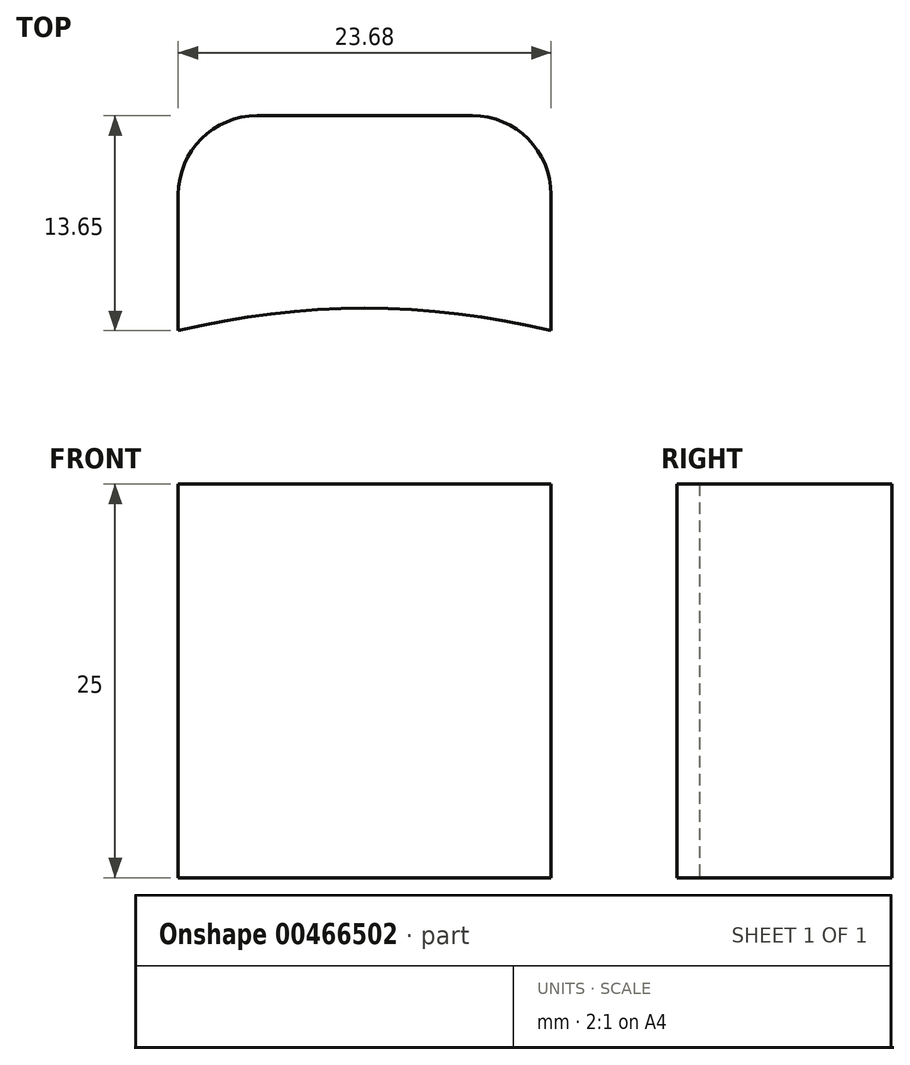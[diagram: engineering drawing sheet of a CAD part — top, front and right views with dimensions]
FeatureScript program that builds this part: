
annotation { "Feature Type Name" : "Feature", "Feature Type Description" : "" }
export const myFeature = defineFeature(function(context is Context, id is Id, definition is map)
    precondition{}
    {
        {
            var Q0;
            Q0=qCreatedBy(makeId("Top.planeOp"),FACE);
            var sketch = newSketch(context, id + "F0", { "sketchPlane" : qUnion([Q0])});
            skCircle(sketch, "E0", {"center": v(-6.85, -8.47) * mm, "radius": 17.48 * mm});
            skCircle(sketch, "E1", {"center": v(-6.85, -8.47) * mm, "radius": 50.07 * mm});
            skLineSegment(sketch, "E2.bottom", {"start": v(-18.69, 40.18) * mm, "end": v(4.99, 40.18) * mm});
            skLineSegment(sketch, "E2.top", {"start": v(-13.69, 53.83) * mm, "end": v(-0.01, 53.83) * mm});
            skLineSegment(sketch, "E2.left", {"start": v(-18.69, 40.18) * mm, "end": v(-18.69, 48.83) * mm});
            skLineSegment(sketch, "E2.right", {"start": v(4.99, 40.18) * mm, "end": v(4.99, 48.83) * mm});
            skPoint(sketch, "E3.visualSharp", {"position": v(-18.69, 53.83) * mm});
            skArc(sketch, "E3.filletArc", {"start": v(-13.69, 53.83) * mm, "mid": v(-17.22, 52.37) * mm, "end": v(-18.69, 48.83) * mm});
            skPoint(sketch, "E4.visualSharp", {"position": v(4.99, 53.83) * mm});
            skArc(sketch, "E4.filletArc", {"start": v(4.99, 48.83) * mm, "mid": v(3.52, 52.37) * mm, "end": v(-0.01, 53.83) * mm});
            skSolve(sketch);
        }
        {
            var Q0;
            Q0=makeQuery(id+"FwPrpn9WK8tI3X1_0.6.F0.imprint","IMPRINT",FACE,{"disambiguationData":[TD([[makeQuery(id+"FwPrpn9WK8tI3X1_0.6.F0.imprint","IMPRINT",EDGE,{"derivedFrom":sQuery(id+"FwPrpn9WK8tI3X1_0.6.F0.wireOp",EDGE,"E0")}),-1.0]])]});
            var Q1;
            Q1=makeQuery(id+"F0.imprint","IMPRINT",FACE,{"disambiguationData":[TD([[makeQuery(id+"F0.imprint","IMPRINT",EDGE,{"derivedFrom":sQuery(id+"F0.wireOp",EDGE,"E2.top")}),-1.0]])]});
            extrude(context, id + "F1", {"entities" : qUnion([Q0, Q1]), "depth" : 25 * mm});
        }
    });
